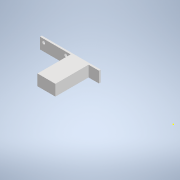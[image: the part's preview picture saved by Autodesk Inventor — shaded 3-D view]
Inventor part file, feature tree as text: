
AUTODESK INVENTOR PART (.ipt)
format: ipt  version: 2022 (Build 260153000, 153)  size: 158,720 bytes
history: native  units: mm
features: reference x4, extrude x3, sketch x3, other x3, projected_geometry x1
ambient origin geometry x8: Origin, YZ Plane, XZ Plane, XY Plane, X Axis, Y Axis, Z Axis, Center Point
bodies: Solid1 (feature_tree)
feature tree (14):
  extrude  "Extrusion1"  Depth=4.0mm
  extrude  "Extrusion2"  Depth=80.0mm
  extrude  "Extrusion3"  Depth=15.0mm
  sketch  "Sketch1"  dims[d0=4.0mm d1=4.0mm]
  reference  "Reference1"
  reference  "Reference2"
  sketch  "Sketch2"  dims[d2=15.0mm d3=80.0mm]
  projected_geometry  "Projected Loop1"
  reference  "Reference3"
  sketch  "Sketch3"  dims[d4=4.5mm d5=5.0mm d6=2.5mm d7=0.0mm d8=10.0mm d9=45.0mm d10=0.0mm d11=9.25mm d12=12.1mm d13=0.2mm d14=1.5mm d15=8.0mm d16=4.0mm d17=1.5mm d18=1.5mm d19=15.0mm d20=0.0mm]
  reference  "Reference4"
  other  "Final_Reduccion.iam"
  other  "Base_proyecto:1"
  other  "motor_12v:1"
